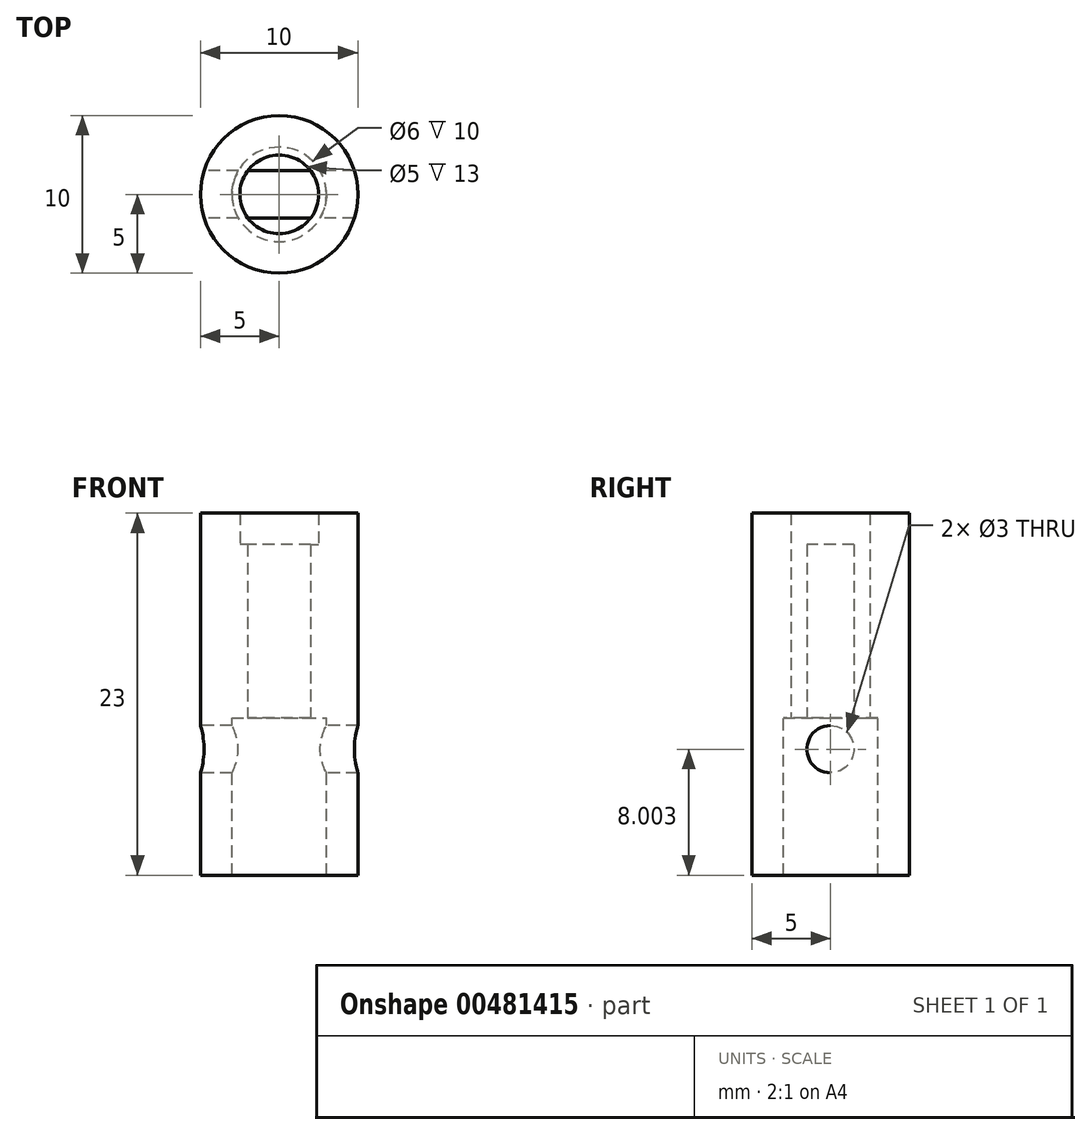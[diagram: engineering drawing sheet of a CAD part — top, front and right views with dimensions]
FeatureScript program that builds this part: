
annotation { "Feature Type Name" : "Feature", "Feature Type Description" : "" }
export const myFeature = defineFeature(function(context is Context, id is Id, definition is map)
    precondition{}
    {
        {
            var Q0;
            Q0=qCreatedBy(makeId("Top.planeOp"),FACE);
            var sketch = newSketch(context, id + "F0", { "sketchPlane" : qUnion([Q0])});
            skCircle(sketch, "E0", {"center": v(0, 0) * mm, "radius": 5 * mm});
            skCircle(sketch, "E1", {"center": v(0, 0) * mm, "radius": 2.5 * mm});
            skCircle(sketch, "E2", {"center": v(0, 0) * mm, "radius": 3 * mm, "construction": true});
            skLineSegment(sketch, "E3.bottom", {"start": v(3.6, -1.5) * mm, "end": v(-3.6, -1.5) * mm});
            skLineSegment(sketch, "E3.top", {"start": v(3.6, 1.5) * mm, "end": v(-3.6, 1.5) * mm});
            skLineSegment(sketch, "E3.left", {"start": v(3.6, -1.5) * mm, "end": v(3.6, 1.5) * mm});
            skLineSegment(sketch, "E3.right", {"start": v(-3.6, -1.5) * mm, "end": v(-3.6, 1.5) * mm});
            skSolve(sketch);
        }
        {
            var Q0;
            Q0=makeQuery(id+"F0.imprint","IMPRINT",FACE,{"disambiguationData":[TD([[makeQuery(id+"F0.imprint","IMPRINT",EDGE,{"derivedFrom":sQuery(id+"F0.wireOp",EDGE,"E0")}),1.0]])]});
            var Q1;
            {var subQ0=sQuery(id+"F0.wireOp",EDGE,"E3.top");var subQ1=sQuery(id+"F0.wireOp",EDGE,"E1");var subQ2=makeQuery(id+"F0.imprint","INTERSECT",VERTEX,{"disambiguationData":[OD(0.0)],"derivedFrom":[subQ1,subQ0]});Q1=makeQuery(id+"F0.imprint","IMPRINT",FACE,{"disambiguationData":[TD([[makeQuery(id+"F0.imprint","IMPRINT",EDGE,{"disambiguationData":[TD([[subQ2,1.0]])],"derivedFrom":subQ1}),1.0]])]});}
            var Q2;
            {var subQ0=sQuery(id+"F0.wireOp",EDGE,"E3.bottom");var subQ1=sQuery(id+"F0.wireOp",EDGE,"E1");var subQ2=makeQuery(id+"F0.imprint","INTERSECT",VERTEX,{"disambiguationData":[OD(0.0)],"derivedFrom":[subQ1,subQ0]});Q2=makeQuery(id+"F0.imprint","IMPRINT",FACE,{"disambiguationData":[TD([[makeQuery(id+"F0.imprint","IMPRINT",EDGE,{"disambiguationData":[TD([[subQ2,-1.0]])],"derivedFrom":subQ1}),1.0]])]});}
            var Q3;
            {var subQ5=sQuery(id+"F0.wireOp",EDGE,"E3.right");Q3=makeQuery(id+"F0.imprint","IMPRINT",FACE,{"disambiguationData":[TD([[makeQuery(id+"F0.imprint","IMPRINT",EDGE,{"derivedFrom":subQ5}),-1.0]])]});}
            var Q4;
            {var subQ5=sQuery(id+"F0.wireOp",EDGE,"E3.left");Q4=makeQuery(id+"F0.imprint","IMPRINT",FACE,{"disambiguationData":[TD([[makeQuery(id+"F0.imprint","IMPRINT",EDGE,{"derivedFrom":subQ5}),1.0]])]});}
            extrude(context, id + "F1", {"entities" : qUnion([Q0, Q1, Q2, Q3, Q4]), "depth" : 7 * mm});
        }
        {
            var Q0;
            Q0=makeQuery(id+"F0.imprint","IMPRINT",FACE,{"disambiguationData":[TD([[makeQuery(id+"F0.imprint","IMPRINT",EDGE,{"derivedFrom":sQuery(id+"F0.wireOp",EDGE,"E0")}),1.0]])]});
            var Q1;
            {var subQ5=sQuery(id+"F0.wireOp",EDGE,"E3.right");Q1=makeQuery(id+"F0.imprint","IMPRINT",FACE,{"disambiguationData":[TD([[makeQuery(id+"F0.imprint","IMPRINT",EDGE,{"derivedFrom":subQ5}),-1.0]])]});}
            var Q2;
            {var subQ5=sQuery(id+"F0.wireOp",EDGE,"E3.left");Q2=makeQuery(id+"F0.imprint","IMPRINT",FACE,{"disambiguationData":[TD([[makeQuery(id+"F0.imprint","IMPRINT",EDGE,{"derivedFrom":subQ5}),1.0]])]});}
            extrude(context, id + "F2", {"entities" : qUnion([Q0, Q1, Q2]), "operationType" : NewBodyOperationType.ADD, "depth" : 9 * mm});
        }
        {
            var Q0;
            Q0=makeQuery(id+"F1.opExtrude","CAP_FACE",FACE,{"disambiguationData":[OSD([sQuery(id+"F0.wireOp",EDGE,"E0"),sQuery(id+"F0.wireOp",EDGE,"E1"),sQuery(id+"F0.wireOp",EDGE,"E3.bottom"),sQuery(id+"F0.wireOp",EDGE,"E3.top")])],"isStart":true});
            var sketch = newSketch(context, id + "F3", { "sketchPlane" : qUnion([Q0])});
            skCircle(sketch, "E4", {"center": v(0, 0) * mm, "radius": 5 * mm});
            skCircle(sketch, "E5", {"center": v(0, 0) * mm, "radius": 3 * mm});
            skSolve(sketch);
        }
        {
            var Q0;
            Q0=makeQuery(id+"F3.imprint","IMPRINT",FACE,{"disambiguationData":[TD([[makeQuery(id+"F3.imprint","IMPRINT",EDGE,{"derivedFrom":sQuery(id+"F3.wireOp",EDGE,"E4")}),-1.0]])]});
            var Q1;
            Q1=makeQuery(id+"F3.imprint","IMPRINT",FACE,{"disambiguationData":[TD([[makeQuery(id+"F3.imprint","IMPRINT",EDGE,{"derivedFrom":sQuery(id+"F3.wireOp",EDGE,"E5")}),1.0]])]});
            var Q2;
            {var subQ2=sQuery(id+"F0.wireOp",EDGE,"E3.bottom");Q2=makeQuery(id+"F3.imprint","IMPRINT",FACE,{"disambiguationData":[TD([[makeQuery(id+"F3.imprint","IMPRINT",EDGE,{"derivedFrom":makeQuery(id+"F1.opExtrude","CAP_EDGE",EDGE,{"disambiguationData":[OSD([subQ2])],"isStart":true})}),1.0]])]});}
            extrude(context, id + "F4", {"entities" : qUnion([Q0, Q1, Q2]), "operationType" : NewBodyOperationType.ADD, "depth" : 4 * mm});
        }
        {
            var Q0;
            Q0=makeQuery(id+"F3.imprint","IMPRINT",FACE,{"disambiguationData":[TD([[makeQuery(id+"F3.imprint","IMPRINT",EDGE,{"derivedFrom":sQuery(id+"F3.wireOp",EDGE,"E4")}),-1.0]])]});
            extrude(context, id + "F5", {"entities" : qUnion([Q0]), "operationType" : NewBodyOperationType.ADD, "depth" : 14 * mm});
        }
        {
            var Q0;
            Q0=qCreatedBy(makeId("Right.planeOp"),FACE);
            var sketch = newSketch(context, id + "F6", { "sketchPlane" : qUnion([Q0])});
            skPoint(sketch, "E6", {"position": v(0, -4) * mm});
            skLineSegment(sketch, "E7", {"start": v(0, -4) * mm, "end": v(0, -6) * mm, "construction": true});
            skCircle(sketch, "E8", {"center": v(0, -6) * mm, "radius": 1.5 * mm});
            skSolve(sketch);
        }
        {
            var Q0;
            Q0=makeQuery(id+"F6.imprint","IMPRINT",FACE,{"disambiguationData":[TD([[makeQuery(id+"F6.imprint","IMPRINT",EDGE,{"derivedFrom":sQuery(id+"F6.wireOp",EDGE,"E8")}),1.0]])]});
            extrude(context, id + "F7", {"entities" : qUnion([Q0]), "operationType" : NewBodyOperationType.REMOVE, "endBound" : BoundingType.SYMMETRIC, "depth" : 25 * mm});
        }
    });
